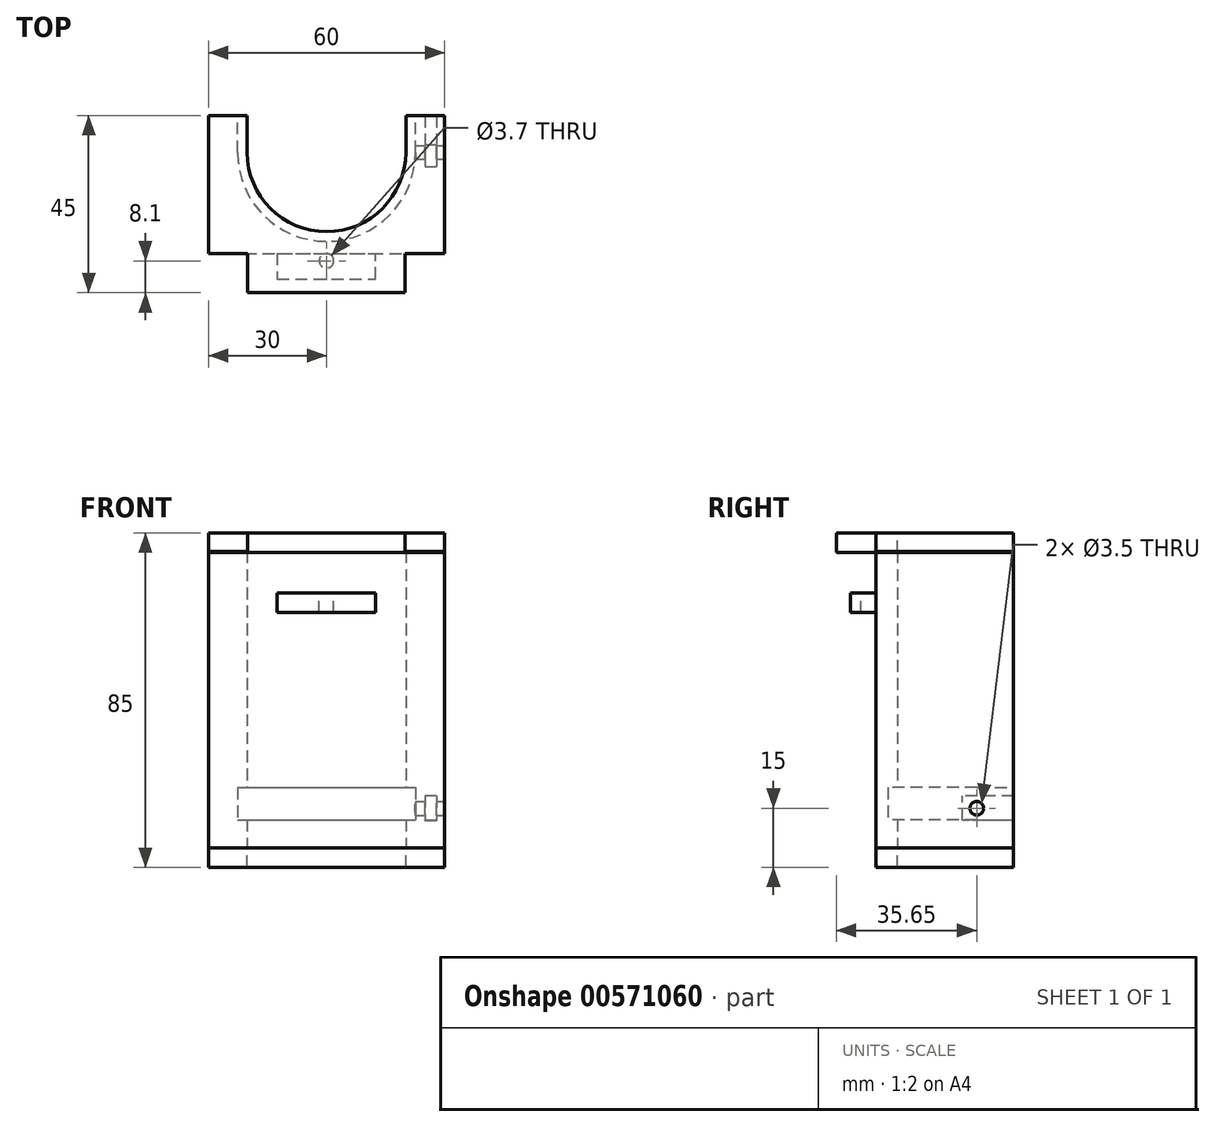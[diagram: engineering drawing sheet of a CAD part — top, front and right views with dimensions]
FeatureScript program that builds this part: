
annotation { "Feature Type Name" : "Feature", "Feature Type Description" : "" }
export const myFeature = defineFeature(function(context is Context, id is Id, definition is map)
    precondition{}
    {
        {
            var Q0;
            Q0=qCreatedBy(makeId("Top.planeOp"),FACE);
            var sketch = newSketch(context, id + "F0", { "sketchPlane" : qUnion([Q0])});
            skLineSegment(sketch, "E0.bottom", {"start": v(-30, 24) * mm, "end": v(-20.15, 24) * mm});
            skLineSegment(sketch, "E0.top", {"start": v(-12.5, -11) * mm, "end": v(30, -11) * mm});
            skLineSegment(sketch, "E0.left", {"start": v(-30, 24) * mm, "end": v(-30, -11) * mm});
            skLineSegment(sketch, "E0.right", {"start": v(30, 24) * mm, "end": v(30, -11) * mm});
            skLineSegment(sketch, "E1.left", {"start": v(-12.5, -17.5) * mm, "end": v(-12.5, -17.5) * mm});
            skLineSegment(sketch, "E1.right", {"start": v(12.5, -17.5) * mm, "end": v(12.5, -17.5) * mm});
            skLineSegment(sketch, "E2.top", {"start": v(12.5, -11) * mm, "end": v(12.5, -11) * mm});
            skLineSegment(sketch, "E3", {"start": v(-30, -11) * mm, "end": v(-12.5, -11) * mm});
            skLineSegment(sketch, "E4", {"start": v(-30, 14.65) * mm, "end": v(30, 14.65) * mm, "construction": true});
            skArc(sketch, "E5", {"start": v(-20.15, 14.65) * mm, "mid": v(0, -5.5) * mm, "end": v(20.15, 14.65) * mm});
            skLineSegment(sketch, "E6", {"start": v(-20.15, 14.65) * mm, "end": v(-20.15, 24) * mm});
            skLineSegment(sketch, "E7", {"start": v(20.15, 14.65) * mm, "end": v(20.15, 24) * mm});
            skLineSegment(sketch, "E8.trimOffspring", {"start": v(20.15, 24) * mm, "end": v(30, 24) * mm});
            skPoint(sketch, "E9.center.orphan", {"position": v(0, -12.9) * mm});
            skSolve(sketch);
        }
        {
            var Q0;
            Q0 = qSketchRegion(id + "F0", true);
            extrude(context, id + "F1", {"entities" : qUnion([Q0]), "depth" : 5 * mm, "offsetDistance" : 25 * mm});
        }
        {
            var Q0;
            Q0=makeQuery(id+"F1.opExtrude","CAP_FACE",FACE,{"disambiguationData":[OSD([sQuery(id+"F0.wireOp",EDGE,"E0.bottom"),sQuery(id+"F0.wireOp",EDGE,"E0.top"),sQuery(id+"F0.wireOp",EDGE,"E0.left"),sQuery(id+"F0.wireOp",EDGE,"E0.right"),sQuery(id+"F0.wireOp",EDGE,"DQeCGjqS-SYIc-2o6I-9SY7-DlFJM7gKKFre.right"),sQuery(id+"F0.wireOp",EDGE,"E1.top"),sQuery(id+"F0.wireOp",EDGE,"E2.right"),sQuery(id+"F0.wireOp",EDGE,"E3"),sQuery(id+"F0.wireOp",EDGE,"E5"),sQuery(id+"F0.wireOp",EDGE,"E6"),sQuery(id+"F0.wireOp",EDGE,"E7"),sQuery(id+"F0.wireOp",EDGE,"E8.trimOffspring")])],"isStart":false});
            var sketch = newSketch(context, id + "F2", { "sketchPlane" : qUnion([Q0])});
            skLineSegment(sketch, "E10.bottom", {"start": v(-30, 24) * mm, "end": v(-20.15, 24) * mm});
            skLineSegment(sketch, "E10.top", {"start": v(-30, -11) * mm, "end": v(30, -11) * mm});
            skLineSegment(sketch, "E10.left", {"start": v(-30, 24) * mm, "end": v(-30, -11) * mm});
            skLineSegment(sketch, "E10.right", {"start": v(30, 24) * mm, "end": v(30, -11) * mm});
            skLineSegment(sketch, "E11.bottom", {"start": v(20.15, 24) * mm, "end": v(20.15, 24) * mm});
            skLineSegment(sketch, "E11.top", {"start": v(20.15, 14.65) * mm, "end": v(20.15, 14.65) * mm});
            skLineSegment(sketch, "E11.left", {"start": v(20.15, 24) * mm, "end": v(20.15, 14.65) * mm});
            skLineSegment(sketch, "E11.right", {"start": v(20.15, 24) * mm, "end": v(20.15, 14.65) * mm});
            skLineSegment(sketch, "E12.bottom", {"start": v(-20.15, 24) * mm, "end": v(-20.15, 24) * mm});
            skLineSegment(sketch, "E12.top", {"start": v(-20.15, 14.65) * mm, "end": v(-20.15, 14.65) * mm});
            skLineSegment(sketch, "E12.left", {"start": v(-20.15, 24) * mm, "end": v(-20.15, 14.65) * mm});
            skLineSegment(sketch, "E12.right", {"start": v(-20.15, 24) * mm, "end": v(-20.15, 14.65) * mm});
            skLineSegment(sketch, "E13.trimOffspring", {"start": v(20.15, 24) * mm, "end": v(30, 24) * mm});
            skArc(sketch, "E14", {"start": v(-20.15, 14.65) * mm, "mid": v(0, -5.5) * mm, "end": v(20.15, 14.65) * mm});
            skSolve(sketch);
        }
        {
            var Q0;
            Q0 = qSketchRegion(id + "F2", true);
            extrude(context, id + "F3", {"entities" : qUnion([Q0]), "operationType" : NewBodyOperationType.ADD, "depth" : 2.1 * mm, "offsetDistance" : 25 * mm});
        }
        {
            var Q0;
            Q0=makeQuery(id+"F3.opExtrude","CAP_FACE",FACE,{"disambiguationData":[OSD([sQuery(id+"F2.wireOp",EDGE,"E10.bottom"),sQuery(id+"F2.wireOp",EDGE,"E10.top"),sQuery(id+"F2.wireOp",EDGE,"E10.left"),sQuery(id+"F2.wireOp",EDGE,"E10.right"),sQuery(id+"F2.wireOp",EDGE,"E11.right"),sQuery(id+"F2.wireOp",EDGE,"E12.right"),sQuery(id+"F2.wireOp",EDGE,"E13.trimOffspring"),sQuery(id+"F2.wireOp",EDGE,"E14")])],"isStart":false});
            var sketch = newSketch(context, id + "F4", { "sketchPlane" : qUnion([Q0])});
            skLineSegment(sketch, "E15.bottom", {"start": v(-30, 24) * mm, "end": v(-22.6, 24) * mm});
            skLineSegment(sketch, "E15.top", {"start": v(-30, -11) * mm, "end": v(30, -11) * mm});
            skLineSegment(sketch, "E15.left", {"start": v(-30, 24) * mm, "end": v(-30, -11) * mm});
            skLineSegment(sketch, "E15.right", {"start": v(30, 24) * mm, "end": v(30, -11) * mm});
            skArc(sketch, "E16", {"start": v(-22.6, 14.65) * mm, "mid": v(0, -7.95) * mm, "end": v(22.6, 14.65) * mm});
            skLineSegment(sketch, "E17", {"start": v(-22.6, 14.65) * mm, "end": v(-22.6, 24) * mm});
            skLineSegment(sketch, "E18", {"start": v(22.6, 14.65) * mm, "end": v(22.6, 24) * mm});
            skLineSegment(sketch, "E19.trimOffspring", {"start": v(22.6, 24) * mm, "end": v(30, 24) * mm});
            skSolve(sketch);
        }
        {
            var Q0;
            Q0 = qSketchRegion(id + "F4", true);
            extrude(context, id + "F5", {"entities" : qUnion([Q0]), "operationType" : NewBodyOperationType.ADD, "depth" : 8.2 * mm, "offsetDistance" : 25 * mm});
        }
        {
            var Q0;
            Q0=makeQuery(id+"F5.opExtrude","CAP_FACE",FACE,{"disambiguationData":[OSD([sQuery(id+"F4.wireOp",EDGE,"E15.bottom"),sQuery(id+"F4.wireOp",EDGE,"E15.top"),sQuery(id+"F4.wireOp",EDGE,"E15.left"),sQuery(id+"F4.wireOp",EDGE,"E15.right"),sQuery(id+"F4.wireOp",EDGE,"E16"),sQuery(id+"F4.wireOp",EDGE,"E17"),sQuery(id+"F4.wireOp",EDGE,"E18"),sQuery(id+"F4.wireOp",EDGE,"E19.trimOffspring")])],"isStart":false});
            var sketch = newSketch(context, id + "F6", { "sketchPlane" : qUnion([Q0])});
            skLineSegment(sketch, "E20.bottom", {"start": v(-30, 24) * mm, "end": v(-20.15, 24) * mm});
            skLineSegment(sketch, "E20.left", {"start": v(-30, 24) * mm, "end": v(-30, -11) * mm});
            skLineSegment(sketch, "E20.right", {"start": v(30, 24) * mm, "end": v(30, -11) * mm});
            skArc(sketch, "E21", {"start": v(-20.15, 14.65) * mm, "mid": v(0, -5.5) * mm, "end": v(20.15, 14.65) * mm});
            skLineSegment(sketch, "E22", {"start": v(-20.15, 14.65) * mm, "end": v(-20.15, 24) * mm});
            skLineSegment(sketch, "E23", {"start": v(20.15, 14.65) * mm, "end": v(20.15, 24) * mm});
            skLineSegment(sketch, "E24.trimOffspring", {"start": v(20.15, 24) * mm, "end": v(30, 24) * mm});
            skLineSegment(sketch, "E25", {"start": v(-30, -11) * mm, "end": v(30, -11) * mm});
            skSolve(sketch);
        }
        {
            var Q0;
            Q0 = qSketchRegion(id + "F6", true);
            var Q1;
            Q1 = qSketchRegion(id + "FYEklNo5dudqzXR_1", true);
            extrude(context, id + "F7", {"entities" : qUnion([Q0, Q1]), "operationType" : NewBodyOperationType.ADD, "depth" : 60 * mm, "offsetDistance" : 25 * mm});
        }
        {
            var Q0;
            Q0=qCreatedBy(makeId("Top.planeOp"),FACE);
            cPlane(context, id + "F8", {"entities" : qUnion([Q0]), "cplaneType" : CPlaneType.OFFSET, "offset" : 80 * mm, "width" : 150 * mm, "height" : 150 * mm});
        }
        {
            var Q0;
            Q0=qCreatedBy(id+"F8.planeOp",FACE);
            var sketch = newSketch(context, id + "F9", { "sketchPlane" : qUnion([Q0])});
            skLineSegment(sketch, "E26.bottom", {"start": v(-30, 24) * mm, "end": v(-20.15, 24) * mm});
            skLineSegment(sketch, "E26.top", {"start": v(-30, -11) * mm, "end": v(-20, -11) * mm});
            skLineSegment(sketch, "E26.left", {"start": v(-30, 24) * mm, "end": v(-30, -11) * mm});
            skLineSegment(sketch, "E26.right", {"start": v(30, 24) * mm, "end": v(30, -11) * mm});
            skLineSegment(sketch, "E27.bottom", {"start": v(20, -21) * mm, "end": v(-20, -21) * mm});
            skLineSegment(sketch, "E27.left", {"start": v(20, -21) * mm, "end": v(20, -11) * mm});
            skLineSegment(sketch, "E27.right", {"start": v(-20, -21) * mm, "end": v(-20, -11) * mm});
            skLineSegment(sketch, "E28.trimOffspring", {"start": v(20, -11) * mm, "end": v(30, -11) * mm});
            skArc(sketch, "E29", {"start": v(-20.15, 14.65) * mm, "mid": v(0, -5.5) * mm, "end": v(20.15, 14.65) * mm});
            skLineSegment(sketch, "E30", {"start": v(-20.15, 14.65) * mm, "end": v(-20.15, 24) * mm});
            skLineSegment(sketch, "E31", {"start": v(20.15, 14.65) * mm, "end": v(20.15, 24) * mm});
            skLineSegment(sketch, "E32.trimOffspring", {"start": v(20.15, 24) * mm, "end": v(30, 24) * mm});
            skSolve(sketch);
        }
        {
            var Q0;
            Q0 = qSketchRegion(id + "F9", true);
            var Q1;
            Q1=makeQuery(id+"F0.imprint","IMPRINT",FACE,{"disambiguationData":[TD([[makeQuery(id+"F0.imprint","IMPRINT",EDGE,{"derivedFrom":sQuery(id+"F0.wireOp",EDGE,"E0.bottom")}),-1.0]])]});
            extrude(context, id + "F10", {"entities" : qUnion([Q0, Q1]), "oppositeDirection" : true, "depth" : 5 * mm, "offsetDistance" : 25 * mm});
        }
        {
            var Q0;
            Q0=qCreatedBy(id+"F8.planeOp",FACE);
            cPlane(context, id + "F11", {"entities" : qUnion([Q0]), "cplaneType" : CPlaneType.OFFSET, "offset" : 15.3 * mm, "oppositeDirection" : true, "width" : 150 * mm, "height" : 150 * mm});
        }
        {
            var Q0;
            Q0=qCreatedBy(id+"F11.planeOp",FACE);
            var sketch = newSketch(context, id + "F12", { "sketchPlane" : qUnion([Q0])});
            skLineSegment(sketch, "E33.top", {"start": v(-12.5, -11) * mm, "end": v(12.5, -11) * mm});
            skLineSegment(sketch, "E34.right", {"start": v(-12.5, -11) * mm, "end": v(-12.5, -17.5) * mm});
            skLineSegment(sketch, "E35.bottom", {"start": v(-12.5, -17.5) * mm, "end": v(12.5, -17.5) * mm});
            skLineSegment(sketch, "E35.top", {"start": v(-12.5, -17.5) * mm, "end": v(12.5, -17.5) * mm});
            skLineSegment(sketch, "E35.left", {"start": v(-12.5, -17.5) * mm, "end": v(-12.5, -17.5) * mm});
            skLineSegment(sketch, "E35.right", {"start": v(12.5, -17.5) * mm, "end": v(12.5, -17.5) * mm});
            skLineSegment(sketch, "E36.top", {"start": v(12.5, -11) * mm, "end": v(12.5, -11) * mm});
            skLineSegment(sketch, "E36.left", {"start": v(12.5, -17.5) * mm, "end": v(12.5, -11) * mm});
            skLineSegment(sketch, "E36.right", {"start": v(12.5, -17.5) * mm, "end": v(12.5, -11) * mm});
            skCircle(sketch, "E37", {"center": v(0, -12.9) * mm, "radius": 1.85 * mm});
            skPoint(sketch, "E38.center.orphan", {"position": v(0, 14.65) * mm});
            skPoint(sketch, "E39.orphan", {"position": v(-20, 14.65) * mm});
            skPoint(sketch, "E40.end.orphan", {"position": v(20, 14.65) * mm});
            skSolve(sketch);
        }
        {
            var Q0;
            Q0 = qSketchRegion(id + "F12", true);
            extrude(context, id + "F13", {"entities" : qUnion([Q0]), "operationType" : NewBodyOperationType.ADD, "oppositeDirection" : true, "depth" : 5 * mm, "offsetDistance" : 25 * mm});
        }
        {
            var Q0;
            Q0=qCreatedBy(makeId("Right.planeOp"),FACE);
            cPlane(context, id + "F14", {"entities" : qUnion([Q0]), "cplaneType" : CPlaneType.OFFSET, "offset" : 25 * mm, "width" : 150 * mm, "height" : 150 * mm});
        }
        {
            var Q0;
            Q0=qCreatedBy(id+"F14.planeOp",FACE);
            var sketch = newSketch(context, id + "F15", { "sketchPlane" : qUnion([Q0])});
            skCircle(sketch, "E41.cCircle", {"center": v(14.65, 10) * mm, "radius": 3.15 * mm, "construction": true});
            skLineSegment(sketch, "E41.0", {"start": v(12.8, 6.86) * mm, "end": v(11.01, 10.03) * mm});
            skLineSegment(sketch, "E41.1", {"start": v(11.01, 10.03) * mm, "end": v(12.85, 13.16) * mm});
            skLineSegment(sketch, "E41.2", {"start": v(12.85, 13.16) * mm, "end": v(16.5, 13.14) * mm});
            skLineSegment(sketch, "E41.3", {"start": v(16.5, 13.14) * mm, "end": v(18.29, 9.97) * mm});
            skLineSegment(sketch, "E41.4", {"start": v(18.29, 9.97) * mm, "end": v(16.45, 6.84) * mm});
            skLineSegment(sketch, "E41.5", {"start": v(16.45, 6.84) * mm, "end": v(12.8, 6.86) * mm});
            skPoint(sketch, "E41.0.midPoint", {"position": v(11.91, 8.44) * mm});
            skCircle(sketch, "E42", {"center": v(14.65, 10) * mm, "radius": 1.75 * mm});
            skSolve(sketch);
        }
        {
            var Q0;
            Q0 = qSketchRegion(id + "F15", true);
            extrude(context, id + "F16", {"entities" : qUnion([Q0]), "operationType" : NewBodyOperationType.REMOVE, "depth" : 3 * mm, "offsetDistance" : 25 * mm});
        }
        {
            var Q0;
            Q0=makeQuery(id+"F7.boolean.opBoolean","MERGE",FACE,{"derivedFrom":[makeQuery(id+"F5.boolean.opBoolean","MERGE",FACE,{"derivedFrom":[makeQuery(id+"F3.boolean.opBoolean","MERGE",FACE,{"derivedFrom":[makeQuery(id+"F1.opExtrude","SWEPT_FACE",FACE,{"disambiguationData":[OSD([sQuery(id+"F0.wireOp",EDGE,"E0.right")])]}),makeQuery(id+"F3.opExtrude","SWEPT_FACE",FACE,{"disambiguationData":[OSD([sQuery(id+"F2.wireOp",EDGE,"E10.right")])]})]}),makeQuery(id+"F5.opExtrude","SWEPT_FACE",FACE,{"disambiguationData":[OSD([sQuery(id+"F4.wireOp",EDGE,"E15.right")])]})]}),makeQuery(id+"F7.opExtrude","SWEPT_FACE",FACE,{"disambiguationData":[OSD([sQuery(id+"F6.wireOp",EDGE,"E20.right")])]})]});
            var sketch = newSketch(context, id + "F17", { "sketchPlane" : qUnion([Q0])});
            skCircle(sketch, "E43", {"center": v(14.65, 10) * mm, "radius": 1.75 * mm});
            skSolve(sketch);
        }
        {
            var Q0;
            Q0 = qSketchRegion(id + "F17", true);
            extrude(context, id + "F18", {"entities" : qUnion([Q0]), "operationType" : NewBodyOperationType.REMOVE, "oppositeDirection" : true, "depth" : 10 * mm, "offsetDistance" : 25 * mm});
        }
        {
            var Q0;
            Q0=qCreatedBy(makeId("Front.planeOp"),FACE);
            var Q1;
            Q1=sQuery(id+"F15.wireOp",VERTEX,"E41.0.end");
            cPlane(context, id + "F19", {"entities" : qUnion([Q0, Q1]), "cplaneType" : CPlaneType.PLANE_POINT, "offset" : 11 * mm, "oppositeDirection" : true, "width" : 150 * mm, "height" : 150 * mm});
        }
        {
            var Q0;
            Q0=qCreatedBy(id+"F19.planeOp",FACE);
            var sketch = newSketch(context, id + "F20", { "sketchPlane" : qUnion([Q0])});
            skLineSegment(sketch, "E44.bottom", {"start": v(25, 6.86) * mm, "end": v(28, 6.86) * mm});
            skLineSegment(sketch, "E44.top", {"start": v(25, 13.16) * mm, "end": v(28, 13.16) * mm});
            skLineSegment(sketch, "E44.left", {"start": v(25, 6.86) * mm, "end": v(25, 13.16) * mm});
            skLineSegment(sketch, "E44.right", {"start": v(28, 6.86) * mm, "end": v(28, 13.16) * mm});
            skSolve(sketch);
        }
        {
            var Q0;
            Q0 = qSketchRegion(id + "F20", true);
            extrude(context, id + "F21", {"entities" : qUnion([Q0]), "operationType" : NewBodyOperationType.REMOVE, "oppositeDirection" : true, "depth" : 25 * mm, "offsetDistance" : 25 * mm});
        }
    });
